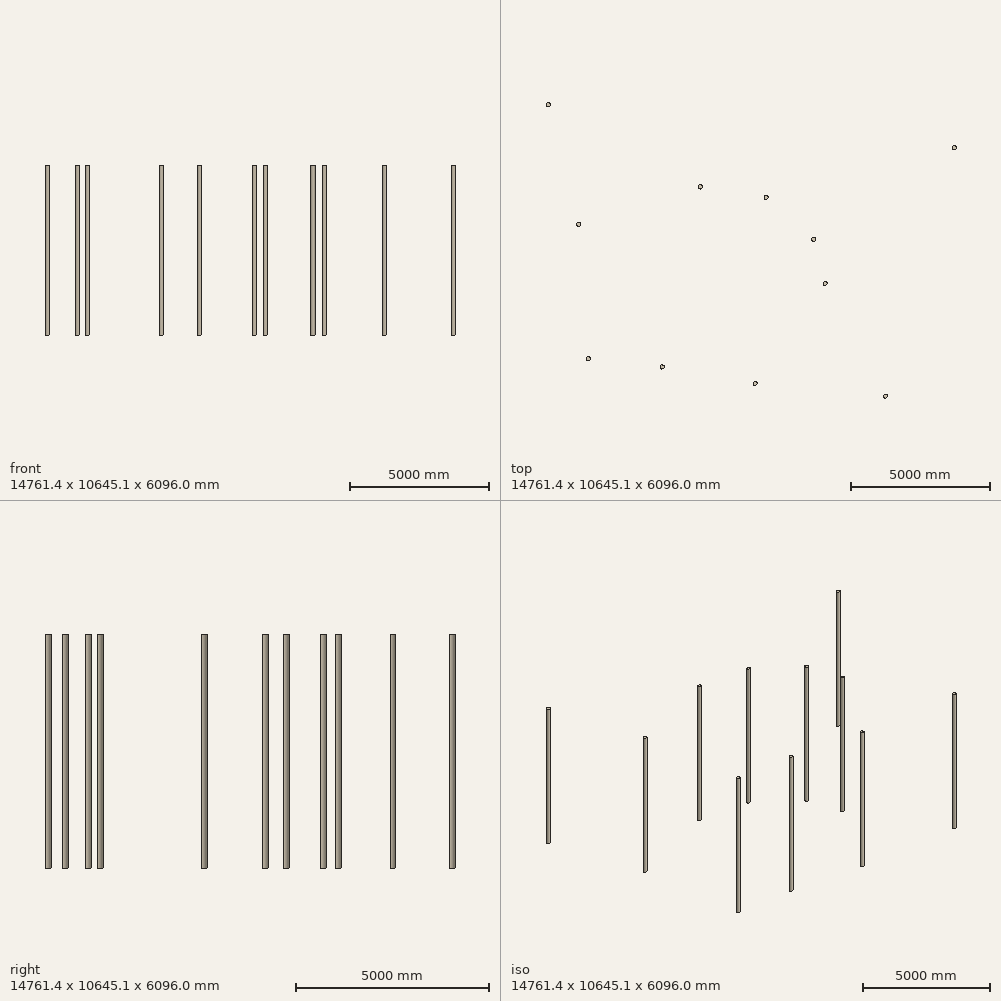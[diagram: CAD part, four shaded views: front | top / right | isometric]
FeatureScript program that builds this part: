
annotation { "Feature Type Name" : "Feature", "Feature Type Description" : "" }
export const myFeature = defineFeature(function(context is Context, id is Id, definition is map)
    precondition{}
    {
        {
            var Q0;
            Q0=qCreatedBy(makeId("Top.planeOp"),FACE);
            var sketch = newSketch(context, id + "F0", { "sketchPlane" : qUnion([Q0])});
            skCircle(sketch, "E0", {"center": v(0, 0) * mm, "radius": 76.2 * mm});
            skCircle(sketch, "E1", {"center": v(-4037.23, -6191.4) * mm, "radius": 76.2 * mm});
            skCircle(sketch, "E2", {"center": v(-1386.2, -6482.85) * mm, "radius": 76.2 * mm});
            skCircle(sketch, "E3", {"center": v(-4393.76, -1353.13) * mm, "radius": 76.2 * mm});
            skCircle(sketch, "E4", {"center": v(2356.88, -381.8) * mm, "radius": 76.2 * mm});
            skCircle(sketch, "E5", {"center": v(4075.98, -1888.61) * mm, "radius": 76.2 * mm});
            skCircle(sketch, "E6", {"center": v(4482.26, -3488.84) * mm, "radius": 76.2 * mm});
            skCircle(sketch, "E7", {"center": v(1962.96, -7089.13) * mm, "radius": 76.2 * mm});
            skCircle(sketch, "E8", {"center": v(6666.34, -7534.32) * mm, "radius": 76.2 * mm});
            skCircle(sketch, "E9", {"center": v(9134.15, 1411.05) * mm, "radius": 76.2 * mm});
            skCircle(sketch, "E10", {"center": v(-5474.8, 2958.41) * mm, "radius": 76.2 * mm});
            skSolve(sketch);
        }
        {
            var Q0;
            Q0 = qSketchRegion(id + "F0", true);
            extrude(context, id + "F1", {"entities" : qUnion([Q0]), "depth" : 6096 * mm, "offsetDistance" : 25.4 * mm});
        }
    });
